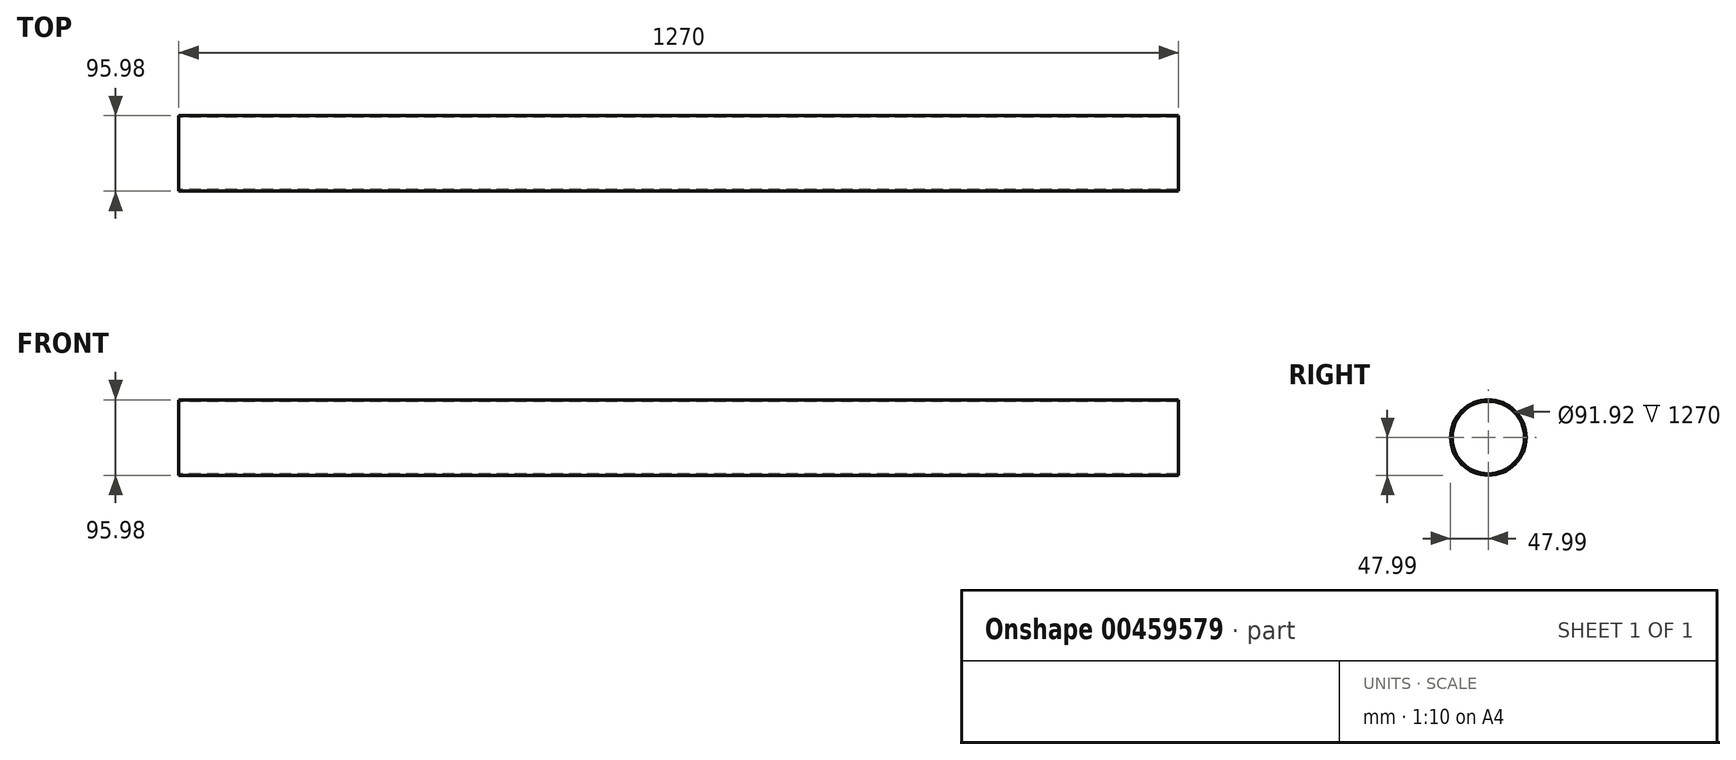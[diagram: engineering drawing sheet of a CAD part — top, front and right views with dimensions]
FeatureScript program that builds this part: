
annotation { "Feature Type Name" : "Feature", "Feature Type Description" : "" }
export const myFeature = defineFeature(function(context is Context, id is Id, definition is map)
    precondition{}
    {
        {
            var Q0;
            Q0=qCreatedBy(makeId("Right.planeOp"),FACE);
            var sketch = newSketch(context, id + "F0", { "sketchPlane" : qUnion([Q0])});
            skCircle(sketch, "E0", {"center": v(0, 0) * mm, "radius": 48 * mm});
            skCircle(sketch, "E1.0", {"center": v(0, 0) * mm, "radius": 45.96 * mm});
            skSolve(sketch);
        }
        {
            var Q0;
            Q0 = qSketchRegion(id + "F0", true);
            extrude(context, id + "F1", {"entities" : qUnion([Q0]), "depth" : 1270 * mm});
        }
    });
